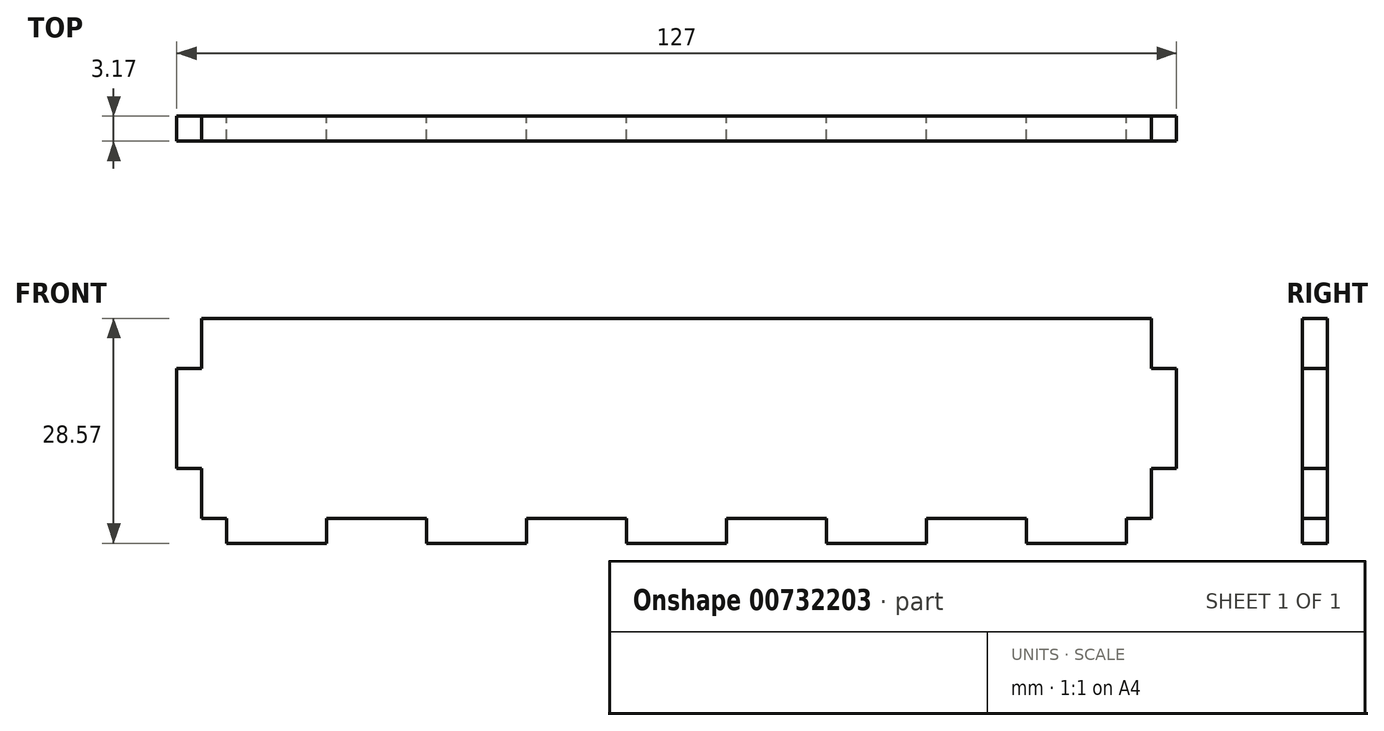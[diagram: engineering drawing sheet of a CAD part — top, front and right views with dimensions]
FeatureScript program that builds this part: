
annotation { "Feature Type Name" : "Feature", "Feature Type Description" : "" }
export const myFeature = defineFeature(function(context is Context, id is Id, definition is map)
    precondition{}
    {
        {
            var Q0;
            Q0=qCreatedBy(makeId("Front.planeOp"),FACE);
            var sketch = newSketch(context, id + "F0", { "sketchPlane" : qUnion([Q0])});
            skLineSegment(sketch, "E0.bottom", {"start": v(-104.85, 13.61) * mm, "end": v(15.8, 13.61) * mm});
            skLineSegment(sketch, "E0.top", {"start": v(-104.85, -11.79) * mm, "end": v(15.8, -11.79) * mm});
            skLineSegment(sketch, "E0.left", {"start": v(-104.85, 13.61) * mm, "end": v(-104.85, -11.79) * mm});
            skLineSegment(sketch, "E0.right", {"start": v(15.8, 13.61) * mm, "end": v(15.8, -11.79) * mm});
            skLineSegment(sketch, "E1", {"start": v(-104.85, -11.79) * mm, "end": v(-101.68, -11.79) * mm});
            skLineSegment(sketch, "E2", {"start": v(-101.68, -11.79) * mm, "end": v(-101.68, -14.96) * mm});
            skLineSegment(sketch, "E3", {"start": v(-101.68, -14.96) * mm, "end": v(-88.98, -14.96) * mm});
            skLineSegment(sketch, "E4", {"start": v(-88.98, -14.96) * mm, "end": v(-88.98, -11.79) * mm});
            skLineSegment(sketch, "E5", {"start": v(-88.98, -11.79) * mm, "end": v(-76.28, -11.79) * mm});
            skLineSegment(sketch, "E6", {"start": v(-76.28, -11.79) * mm, "end": v(-76.28, -14.96) * mm});
            skLineSegment(sketch, "E7", {"start": v(-76.28, -14.96) * mm, "end": v(-63.58, -14.96) * mm});
            skLineSegment(sketch, "E8", {"start": v(-63.58, -14.96) * mm, "end": v(-63.58, -11.79) * mm});
            skLineSegment(sketch, "E9", {"start": v(-63.58, -11.79) * mm, "end": v(-50.88, -11.79) * mm});
            skLineSegment(sketch, "E10", {"start": v(-50.88, -11.79) * mm, "end": v(-50.88, -14.96) * mm});
            skLineSegment(sketch, "E11", {"start": v(-50.88, -14.96) * mm, "end": v(-38.18, -14.96) * mm});
            skLineSegment(sketch, "E12", {"start": v(-38.18, -14.96) * mm, "end": v(-38.18, -11.79) * mm});
            skLineSegment(sketch, "E13", {"start": v(-38.18, -11.79) * mm, "end": v(-25.48, -11.79) * mm});
            skLineSegment(sketch, "E14", {"start": v(-25.48, -11.79) * mm, "end": v(-25.48, -14.96) * mm});
            skLineSegment(sketch, "E15", {"start": v(-25.48, -14.96) * mm, "end": v(-12.78, -14.96) * mm});
            skLineSegment(sketch, "E16", {"start": v(-12.78, -14.96) * mm, "end": v(-12.78, -11.79) * mm});
            skLineSegment(sketch, "E17", {"start": v(-12.78, -11.79) * mm, "end": v(-0.08, -11.79) * mm});
            skLineSegment(sketch, "E18", {"start": v(-0.08, -11.79) * mm, "end": v(-0.08, -14.96) * mm});
            skLineSegment(sketch, "E19", {"start": v(-0.08, -14.96) * mm, "end": v(12.62, -14.96) * mm});
            skLineSegment(sketch, "E20", {"start": v(12.62, -14.96) * mm, "end": v(12.62, -11.79) * mm});
            skLineSegment(sketch, "E21", {"start": v(12.62, -11.79) * mm, "end": v(25.32, -11.79) * mm});
            skLineSegment(sketch, "E22", {"start": v(-104.85, 13.61) * mm, "end": v(-104.85, 7.26) * mm});
            skLineSegment(sketch, "E23", {"start": v(-104.85, 7.26) * mm, "end": v(-108.03, 7.26) * mm});
            skLineSegment(sketch, "E24", {"start": v(-108.03, 7.26) * mm, "end": v(-108.03, -5.44) * mm});
            skLineSegment(sketch, "E25", {"start": v(-108.03, -5.44) * mm, "end": v(-104.85, -5.44) * mm});
            skLineSegment(sketch, "E26", {"start": v(15.8, 13.61) * mm, "end": v(15.8, 7.26) * mm});
            skLineSegment(sketch, "E27", {"start": v(15.8, 7.26) * mm, "end": v(18.97, 7.26) * mm});
            skLineSegment(sketch, "E28", {"start": v(18.97, 7.26) * mm, "end": v(18.97, -5.44) * mm});
            skLineSegment(sketch, "E29", {"start": v(18.97, -5.44) * mm, "end": v(15.8, -5.44) * mm});
            skSolve(sketch);
        }
        {
            var Q0;
            {var subQ10=sQuery(id+"F0.wireOp",EDGE,"E0.bottom");Q0=makeQuery(id+"F0.imprint","IMPRINT",FACE,{"disambiguationData":[TD([[makeQuery(id+"F0.imprint","IMPRINT",EDGE,{"derivedFrom":subQ10}),-1.0]])]});}
            var Q1;
            {var subQ0=sQuery(id+"F0.wireOp",EDGE,"E10");Q1=makeQuery(id+"F0.imprint","IMPRINT",FACE,{"disambiguationData":[TD([[makeQuery(id+"F0.imprint","IMPRINT",EDGE,{"derivedFrom":subQ0}),1.0]])]});}
            var Q2;
            {var subQ0=sQuery(id+"F0.wireOp",EDGE,"E14");Q2=makeQuery(id+"F0.imprint","IMPRINT",FACE,{"disambiguationData":[TD([[makeQuery(id+"F0.imprint","IMPRINT",EDGE,{"derivedFrom":subQ0}),1.0]])]});}
            var Q3;
            {var subQ2=sQuery(id+"F0.wireOp",EDGE,"E2");Q3=makeQuery(id+"F0.imprint","IMPRINT",FACE,{"disambiguationData":[TD([[makeQuery(id+"F0.imprint","IMPRINT",EDGE,{"derivedFrom":subQ2}),1.0]])]});}
            var Q4;
            {var subQ0=sQuery(id+"F0.wireOp",EDGE,"E6");Q4=makeQuery(id+"F0.imprint","IMPRINT",FACE,{"disambiguationData":[TD([[makeQuery(id+"F0.imprint","IMPRINT",EDGE,{"derivedFrom":subQ0}),1.0]])]});}
            var Q5;
            {var subQ0=sQuery(id+"F0.wireOp",EDGE,"E18");Q5=makeQuery(id+"F0.imprint","IMPRINT",FACE,{"disambiguationData":[TD([[makeQuery(id+"F0.imprint","IMPRINT",EDGE,{"derivedFrom":subQ0}),1.0]])]});}
            var Q6;
            {var subQ0=sQuery(id+"F0.wireOp",EDGE,"gVpqYOuL-59UL-0vWp-yV1u-nPBN169zkQMX");Q6=makeQuery(id+"F0.imprint","IMPRINT",FACE,{"disambiguationData":[TD([[makeQuery(id+"F0.imprint","IMPRINT",EDGE,{"derivedFrom":subQ0}),1.0]])]});}
            var Q7;
            {var subQ0=sQuery(id+"F0.wireOp",EDGE,"E23");Q7=makeQuery(id+"F0.imprint","IMPRINT",FACE,{"disambiguationData":[TD([[makeQuery(id+"F0.imprint","IMPRINT",EDGE,{"derivedFrom":subQ0}),1.0]])]});}
            var Q8;
            {var subQ0=sQuery(id+"F0.wireOp",EDGE,"E27");Q8=makeQuery(id+"F0.imprint","IMPRINT",FACE,{"disambiguationData":[TD([[makeQuery(id+"F0.imprint","IMPRINT",EDGE,{"derivedFrom":subQ0}),-1.0]])]});}
            extrude(context, id + "F1", {"entities" : qUnion([Q0, Q1, Q2, Q3, Q4, Q5, Q6, Q7, Q8]), "depth" : 3.17 * mm, "offsetDistance" : 25.4 * mm});
        }
    });
